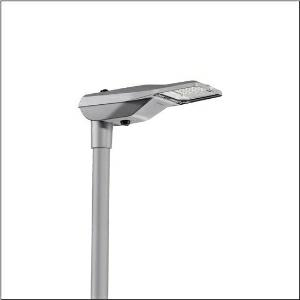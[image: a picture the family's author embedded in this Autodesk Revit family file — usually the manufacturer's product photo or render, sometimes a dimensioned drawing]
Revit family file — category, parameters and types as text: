
# Revit family: streetlight_sl_21_iq_micro___st1_0a_5xe1d51y08cb_5320
name_source: partatom
category: Lighting Fixtures
units: mm (PartAtom-declared; Revit-internal decimal feet)

## family parameters
Cut with Voids When Loaded = No
Host = Face
Light Source = No
Part Type = Normal
Room Calculation Point = No
Round Connector Dimension = Use Diameter
Shared = No

## types (1)
- --- (1 x LED, 2530 lm, 19.1 W, 3000K)
    Apparent Load = 19 VA
    CIE Flux Codes = 37 72 97 100 100
    Color Rendering = 80
    Color Temperature = 3000K
    Default Elevation = 1800 mm
    Description = Streetlight SL 21 iQ micro, mast luminaire, primary light control with lens, of PMMA, primary optical cover: cover, of toughened safety glass, transparent, light distribution: ST1.0a, light emission: direct distribution, primary light characteristic: asymmetric, installation type: post-top, side-entry, LED, High Power LED, rated luminous flux: 2.530lm, luminous efficacy: 133lm/W, light colour: 830, colour temperature: 3000K, control gear: iQ-Street Remote, D4i with power reduction, control: pre-setting: logarithmic dimming characteristic, Street-Remote, Auto-Match, Temp-Guard, Lumen-Switch, Night-Set, Smart-Wire, Light-Fading, Desk-Remote (wireless, voltage-free reading and setting of iQ features in the workshop via application-optimized NFC function/RFID function), optimised constant luminous flux control (CLO 2.0), mains connection: 220..240V, AC, 50/60Hz, start of lifetime: 19W, end of service life: 20W, reduction: 9W, luminaire housing, of diecast aluminium, powder-coated, Siteco® metallic grey (DB 702S), corrosivity category C5 mid according to DIN EN ISO 12944, please order mast flange separately, inclination adjustable: 0°, 5°, 10°, 15°, sealing non-destructively replaceable, multi-level sealing system, length: 528mm, width: 235mm, height: 110mm, mast flange for spigot size: 42mm (side-entry): 5XC10008XM4, 60/48mm (side-entry/post-top): 5XC10108XM2, 76/60mm (side-entry/post-top): 5XC10108XM1, mounting height: 4..8m, Smart Interface below and above, protection rating (complete): IP66, insulation class (complete): insulation class II (safety insulation), certification: CE, ENEC, ENEC+, VDE, impact resistance: IK10, permissible operating ambient temperature for outdoor applications: -40..+50°C, standard-compliant lighting for roads and squares, packaging unit: 1 piece

Light Distribution: ST1.0a
    Height = 110 mm
    Lamp = 1 x LED
    Lamp Light Flux = 2530 lm
    Lamp Power = 19.1 W
    Lamp count = 1
    Length = 528 mm
    Luminous efficacy = 132 lm/W
    Manufacturer = Siteco
    ModVariant = No
    Model = 5XE1D51Y08CB
    Number of Poles = 1
    OnlyDefault = Yes
    Power Factor = 1
    Product Name = Streetlight SL 21 iQ micro | ST1.0a
    Product group = mast luminaire | pylon top
    ProductGroupID = 6100
    Protection Class = Protection class II
    Protection Degree = IP 66
    RLX_Detail_Level = 1
    RLX_Emergency_Light_Flux = 0 lm
    RLX_Emergency_Type = 0
    RLX_Emergency_Type_DB = No
    RlxData = <blob elided: 98489 chars, md5=d54b8160>
    Socket = socket
    Standby Power = 0 W
    System Light Flux = 2530 lm
    System Power = 19 W
    Type Comments = factory setting: luminous flux: 100 % | dim-lin: 254 | 387 mA
    Type Image = l_1007239.jpg
    URL = http://relux.com
    VarID = @adj_136857
    Voltage = 0 V
    Weight = 0.00 kg
    Width = 235 mm

## geometry (parser evidence)
native form markers: Blend x4, Sweep x11
no freeform markers — native parametric forms only
